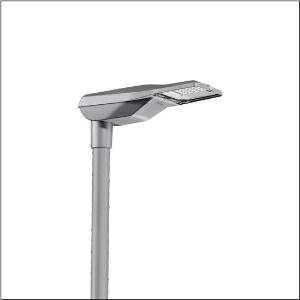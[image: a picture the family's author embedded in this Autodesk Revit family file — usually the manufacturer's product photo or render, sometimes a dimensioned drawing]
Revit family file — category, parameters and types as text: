
# Revit family: streetlight_sl_21_iq_micro___st1_0a_5xe1d41g08db_b7c0
name_source: partatom
category: Lighting Fixtures
units: mm (PartAtom-declared; Revit-internal decimal feet)

## family parameters
Cut with Voids When Loaded = No
Host = Face
Light Source = No
Part Type = Normal
Room Calculation Point = No
Round Connector Dimension = Use Diameter
Shared = No

## types (1)
- --- (1 x LED, 5010 lm, 36.4 W, 4000K)
    Apparent Load = 36 VA
    CIE Flux Codes = 37 72 97 100 100
    Color Rendering = 70
    Color Temperature = 4000K
    Default Elevation = 1800 mm
    Description = Streetlight SL 21 iQ micro, mast luminaire, primary light control with lens, of PMMA, primary optical cover: cover, of toughened safety glass, transparent, light distribution: ST1.0a, light emission: direct distribution, primary light characteristic: asymmetric, installation type: post-top, side-entry, LED, High Power LED, rated luminous flux: 5.010lm, luminous efficacy: 138lm/W, light colour: 740, colour temperature: 4000K, control: Street-Remote, Auto-Match, Temp-Guard, Lumen-Switch, Night-Set, Smart-Wire, Light-Fading, Desk-Remote (wireless, voltage-free reading and setting of iQ features in the workshop via application-optimized NFC function/RFID function), optimised constant luminous flux control (CLO 2.0), presetting dimming linear, mains connection: 220..240V, AC, 50/60Hz, start of lifetime: 36W, end of service life: 38W, reduction: 16W, luminaire housing, of diecast aluminium, powder-coated, Siteco® metallic grey (DB 702S), corrosivity category C5 mid according to DIN EN ISO 12944, please order mast flange separately, inclination adjustable: 0°, 5°, 10°, 15°, sealing non-destructively replaceable, multi-level sealing system, length: 528mm, width: 235mm, height: 110mm, mast flange for spigot size: 42mm (side-entry): 5XC10008XM4, 60/48mm (side-entry/post-top): 5XC10108XM2, 76/60mm (side-entry/post-top): 5XC10108XM1, protection rating (complete): IP66, insulation class (complete): insulation class II (safety insulation), certification: CE, ENEC, ENEC+, VDE, impact resistance: IK09, permissible operating ambient temperature for outdoor applications: -40..+50°C, standard-compliant lighting for roads and squares, packaging unit: 1 piece

Light Distribution: ST1.0a
    Height = 110 mm
    Lamp = 1 x LED
    Lamp Light Flux = 5010 lm
    Lamp Power = 36.4 W
    Lamp count = 1
    Length = 528 mm
    Luminous efficacy = 138 lm/W
    Manufacturer = Siteco
    ModVariant = No
    Model = 5XE1D41G08DB
    Number of Poles = 1
    OnlyDefault = Yes
    Power Factor = 1
    Product Name = Streetlight SL 21 iQ micro | ST1.0a
    Product group = mast luminaire | pylon top
    ProductGroupID = 6100
    Protection Class = Protection class II
    Protection Degree = IP 66
    RLX_Detail_Level = 1
    RLX_Emergency_Light_Flux = 0 lm
    RLX_Emergency_Type = 0
    RLX_Emergency_Type_DB = No
    RlxData = <blob elided: 99501 chars, md5=057aff87>
    Socket = socket
    Standby Power = 0 W
    System Light Flux = 5010 lm
    System Power = 36 W
    Type Comments = factory setting: luminous flux: 100 % | dim-lin: 254 | 715 mA
    Type Image = l_1006881.jpg
    URL = http://relux.com
    VarID = @adj_088215
    Voltage = 0 V
    Weight = 0.00 kg
    Width = 235 mm

## geometry (parser evidence)
native form markers: Blend x4, Sweep x10
no freeform markers — native parametric forms only
